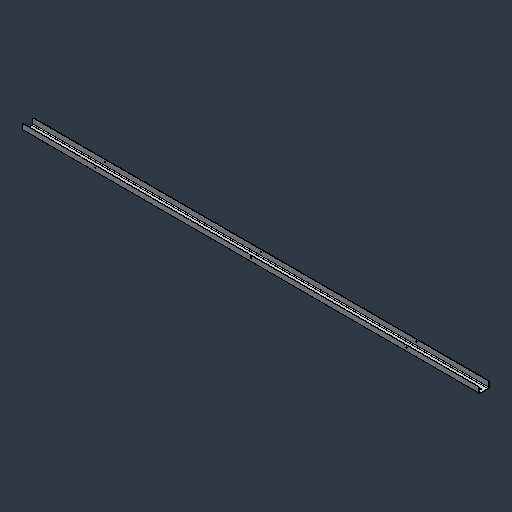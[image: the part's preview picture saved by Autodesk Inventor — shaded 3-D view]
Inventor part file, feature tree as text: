
AUTODESK INVENTOR PART (.ipt)
format: ipt  version: 2024.3 (Build 283343000, 343)  size: 104,960 bytes
history: native  units: mm (DEFAULTED — no unit token found)
features: fillet x1
ambient origin geometry x8: Origin, YZ Plane, XZ Plane, XY Plane, X Axis, Y Axis, Z Axis, Center Point
bodies: Solid1 (feature_tree)
feature tree (1):
  fillet  "Fillet1"  [1 undecoded]
note: 1 required parameter value undecoded (feature->parameter linkage not recoverable at this tier; creation-order binding heuristic only, values carry confidence <= 0.55)
